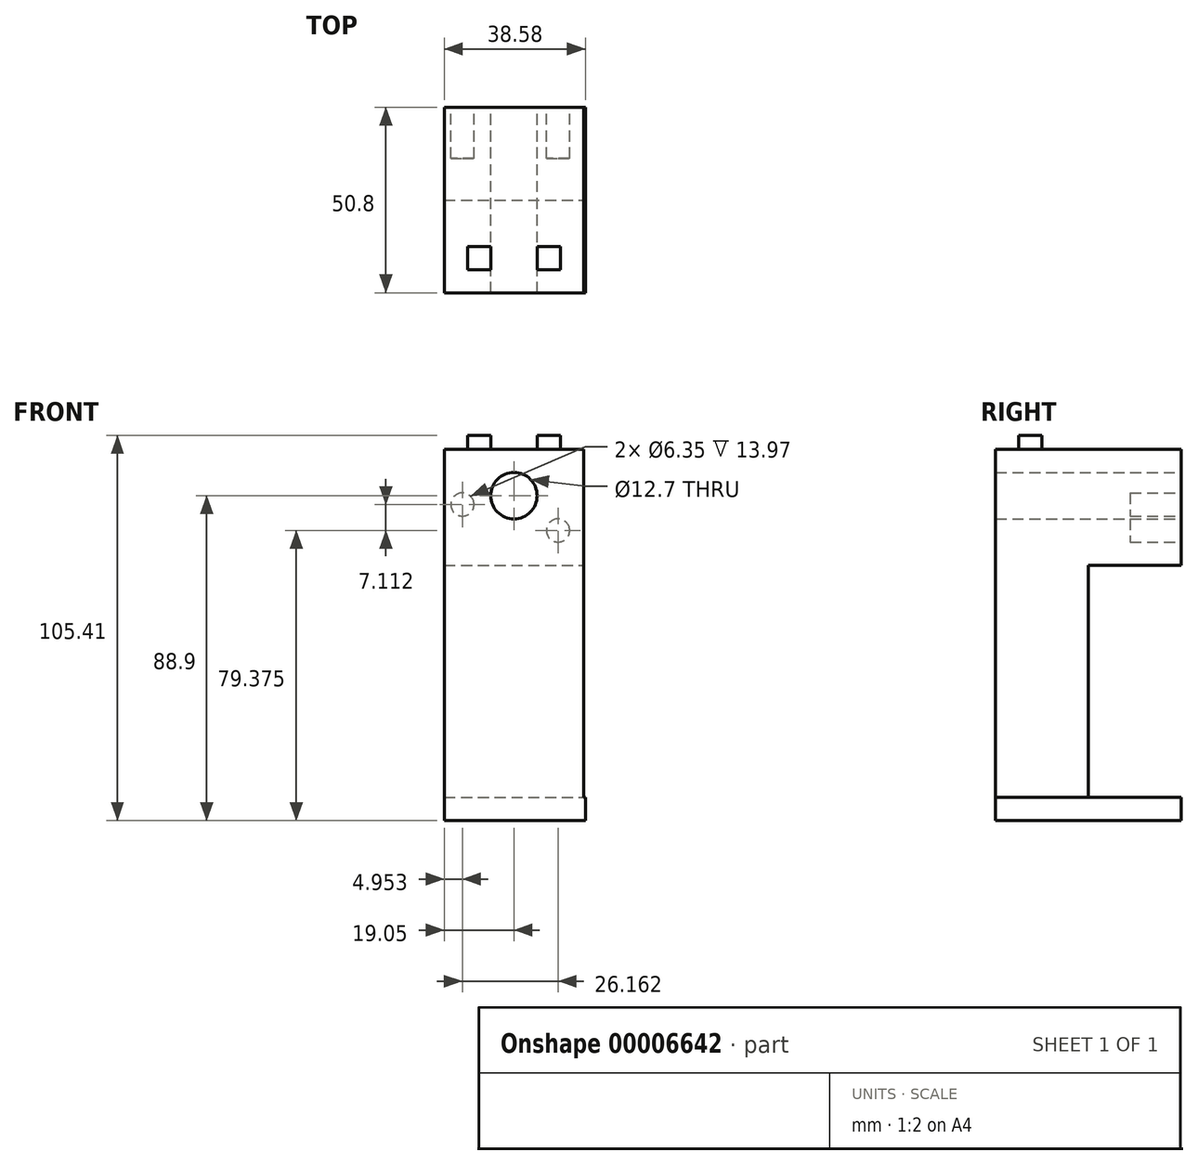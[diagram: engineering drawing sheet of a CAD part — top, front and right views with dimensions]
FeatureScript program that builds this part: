
annotation { "Feature Type Name" : "Feature", "Feature Type Description" : "" }
export const myFeature = defineFeature(function(context is Context, id is Id, definition is map)
    precondition{}
    {
        {
            var Q0;
            Q0=qCreatedBy(makeId("Front.planeOp"),FACE);
            var sketch = newSketch(context, id + "F0", { "sketchPlane" : qUnion([Q0])});
            skLineSegment(sketch, "E0.bottom", {"start": v(-19.05, 2.54) * mm, "end": v(19.05, 2.54) * mm});
            skLineSegment(sketch, "E0.top", {"start": v(-19.05, -19.05) * mm, "end": v(19.05, -19.05) * mm});
            skLineSegment(sketch, "E0.left", {"start": v(-19.05, 2.54) * mm, "end": v(-19.05, -19.05) * mm});
            skLineSegment(sketch, "E0.right", {"start": v(19.05, 2.54) * mm, "end": v(19.05, -19.05) * mm});
            skSolve(sketch);
        }
        {
            var Q0;
            Q0 = qSketchRegion(id + "F0", true);
            extrude(context, id + "F1", {"entities" : qUnion([Q0]), "depth" : 50.8 * mm});
        }
        {
            var Q0;
            Q0=makeQuery(id+"F1.opExtrude","CAP_FACE",FACE,{"disambiguationData":[OSD([sQuery(id+"F0.wireOp",EDGE,"E0.bottom"),sQuery(id+"F0.wireOp",EDGE,"E0.top"),sQuery(id+"F0.wireOp",EDGE,"E0.left"),sQuery(id+"F0.wireOp",EDGE,"E0.right")])],"isStart":true});
            var sketch = newSketch(context, id + "F2", { "sketchPlane" : qUnion([Q0])});
            skCircle(sketch, "E1", {"center": v(14.1, -2.41) * mm, "radius": 3.18 * mm});
            skCircle(sketch, "E2", {"center": v(-12.06, -9.52) * mm, "radius": 3.18 * mm});
            skSolve(sketch);
        }
        {
            var Q0;
            Q0 = qSketchRegion(id + "F2", true);
            extrude(context, id + "F3", {"entities" : qUnion([Q0]), "operationType" : NewBodyOperationType.REMOVE, "oppositeDirection" : true, "depth" : 13.97 * mm});
        }
        {
            var Q0;
            Q0=makeQuery(id+"F1.opExtrude","SWEPT_FACE",FACE,{"disambiguationData":[OSD([sQuery(id+"F0.wireOp",EDGE,"E0.top")])]});
            var sketch = newSketch(context, id + "F4", { "sketchPlane" : qUnion([Q0])});
            skLineSegment(sketch, "E3.bottom", {"start": v(-19.05, 50.8) * mm, "end": v(19.05, 50.8) * mm});
            skLineSegment(sketch, "E3.top", {"start": v(-19.05, 25.4) * mm, "end": v(19.05, 25.4) * mm});
            skLineSegment(sketch, "E3.left", {"start": v(-19.05, 50.8) * mm, "end": v(-19.05, 25.4) * mm});
            skLineSegment(sketch, "E3.right", {"start": v(19.05, 50.8) * mm, "end": v(19.05, 25.4) * mm});
            skSolve(sketch);
        }
        {
            var Q0;
            Q0 = qSketchRegion(id + "F4", true);
            extrude(context, id + "F5", {"entities" : qUnion([Q0]), "operationType" : NewBodyOperationType.ADD, "depth" : 63.5 * mm});
        }
        {
            var Q0;
            Q0=makeQuery(id+"F5.opExtrude","CAP_FACE",FACE,{"disambiguationData":[OSD([sQuery(id+"F4.wireOp",EDGE,"E3.bottom"),sQuery(id+"F4.wireOp",EDGE,"E3.top"),sQuery(id+"F4.wireOp",EDGE,"E3.left"),sQuery(id+"F4.wireOp",EDGE,"E3.right")])],"isStart":false});
            var sketch = newSketch(context, id + "F6", { "sketchPlane" : qUnion([Q0])});
            skLineSegment(sketch, "E4.bottom", {"start": v(-19.05, 50.8) * mm, "end": v(19.53, 50.8) * mm});
            skLineSegment(sketch, "E4.top", {"start": v(-19.05, 0) * mm, "end": v(19.53, 0) * mm});
            skLineSegment(sketch, "E4.left", {"start": v(-19.05, 50.8) * mm, "end": v(-19.05, 0) * mm});
            skLineSegment(sketch, "E4.right", {"start": v(19.53, 50.8) * mm, "end": v(19.53, 0) * mm});
            skSolve(sketch);
        }
        {
            var Q0;
            Q0 = qSketchRegion(id + "F6", true);
            extrude(context, id + "F7", {"entities" : qUnion([Q0]), "operationType" : NewBodyOperationType.ADD, "depth" : 6.35 * mm});
        }
        {
            var Q0;
            Q0=makeQuery(id+"F1.opExtrude","CAP_FACE",FACE,{"disambiguationData":[OSD([sQuery(id+"F0.wireOp",EDGE,"E0.bottom"),sQuery(id+"F0.wireOp",EDGE,"E0.top"),sQuery(id+"F0.wireOp",EDGE,"E0.left"),sQuery(id+"F0.wireOp",EDGE,"E0.right")])],"isStart":true});
            var sketch = newSketch(context, id + "F8", { "sketchPlane" : qUnion([Q0])});
            skLineSegment(sketch, "E5.bottom", {"start": v(-19.05, 2.54) * mm, "end": v(19.05, 2.54) * mm});
            skLineSegment(sketch, "E5.top", {"start": v(-19.05, 12.7) * mm, "end": v(19.05, 12.7) * mm});
            skLineSegment(sketch, "E5.left", {"start": v(-19.05, 2.54) * mm, "end": v(-19.05, 12.7) * mm});
            skLineSegment(sketch, "E5.right", {"start": v(19.05, 2.54) * mm, "end": v(19.05, 12.7) * mm});
            skSolve(sketch);
        }
        {
            var Q0;
            Q0 = qSketchRegion(id + "F8", true);
            extrude(context, id + "F9", {"entities" : qUnion([Q0]), "operationType" : NewBodyOperationType.ADD, "oppositeDirection" : true, "depth" : 50.8 * mm});
        }
        {
            var Q0;
            Q0=makeQuery(id+"F1.opExtrude","CAP_FACE",FACE,{"disambiguationData":[OSD([sQuery(id+"F0.wireOp",EDGE,"E0.bottom"),sQuery(id+"F0.wireOp",EDGE,"E0.top"),sQuery(id+"F0.wireOp",EDGE,"E0.left"),sQuery(id+"F0.wireOp",EDGE,"E0.right")])],"isStart":true});
            var sketch = newSketch(context, id + "F10", { "sketchPlane" : qUnion([Q0])});
            skCircle(sketch, "E6", {"center": v(0, 0) * mm, "radius": 6.35 * mm});
            skSolve(sketch);
        }
        {
            var Q0;
            Q0 = qSketchRegion(id + "F10", true);
            extrude(context, id + "F11", {"entities" : qUnion([Q0]), "operationType" : NewBodyOperationType.REMOVE, "oppositeDirection" : true, "depth" : 50.8 * mm});
        }
        {
            var Q0;
            Q0=makeQuery(id+"F9.opExtrude","SWEPT_FACE",FACE,{"disambiguationData":[OSD([sQuery(id+"F8.wireOp",EDGE,"E5.top")])]});
            var sketch = newSketch(context, id + "F12", { "sketchPlane" : qUnion([Q0])});
            skLineSegment(sketch, "E7.bottom", {"start": v(-12.7, -38.1) * mm, "end": v(-6.35, -38.1) * mm});
            skLineSegment(sketch, "E7.top", {"start": v(-12.7, -44.45) * mm, "end": v(-6.35, -44.45) * mm});
            skLineSegment(sketch, "E7.left", {"start": v(-12.7, -38.1) * mm, "end": v(-12.7, -44.45) * mm});
            skLineSegment(sketch, "E7.right", {"start": v(-6.35, -38.1) * mm, "end": v(-6.35, -44.45) * mm});
            skLineSegment(sketch, "E8.bottom", {"start": v(6.35, -38.1) * mm, "end": v(12.7, -38.1) * mm});
            skLineSegment(sketch, "E8.top", {"start": v(6.35, -44.45) * mm, "end": v(12.7, -44.45) * mm});
            skLineSegment(sketch, "E8.left", {"start": v(6.35, -38.1) * mm, "end": v(6.35, -44.45) * mm});
            skLineSegment(sketch, "E8.right", {"start": v(12.7, -38.1) * mm, "end": v(12.7, -44.45) * mm});
            skSolve(sketch);
        }
        {
            var Q0;
            Q0 = qSketchRegion(id + "F12", true);
            extrude(context, id + "F13", {"entities" : qUnion([Q0]), "operationType" : NewBodyOperationType.ADD, "depth" : 3.8 * mm});
        }
    });
